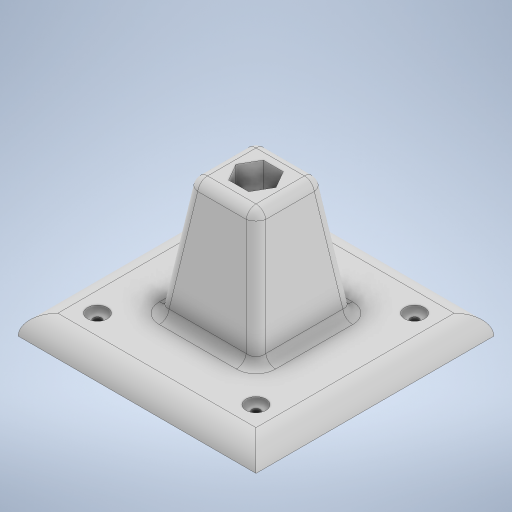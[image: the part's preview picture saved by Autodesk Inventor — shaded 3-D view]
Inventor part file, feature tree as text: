
AUTODESK INVENTOR PART (.ipt)
format: ipt  version: 2023 (Build 270158000, 158)  size: 339,968 bytes
history: native  units: mm
features: extrude x4, chamfer x4, sketch x4, fillet x3, other x1
ambient origin geometry x8: Origin, YZ Plane, XZ Plane, XY Plane, X Axis, Y Axis, Z Axis, Center Point
bodies: Body1 (feature_tree)
feature tree (16):
  other  "Bryła1"
  extrude  "Wyciągnięcie proste1"  Depth=120.0mm
  extrude  "Wyciągnięcie proste2"  Depth=120.0mm
  extrude  "Wyciągnięcie proste3"  Depth=10.0mm TaperAngle=0.0deg
  chamfer  "Faza5"  Distance=50.0mm
  chamfer  "Faza6"  Distance=50.0mm
  chamfer  "Faza7"  Distance=60.0mm
  chamfer  "Faza8"  Distance=17.5mm
  fillet  "Zaokrąglenie1"  Radius=50.0mm
  fillet  "Zaokrąglenie2"  Radius=2.0mm
  extrude  "Wyciągnięcie proste4"  Depth=2.0mm
  fillet  "Zaokrąglenie3"  Radius=2.0mm
  sketch  "Szkic1"
  sketch  "Szkic2"
  sketch  "Szkic3"
  sketch  "Szkic4"
